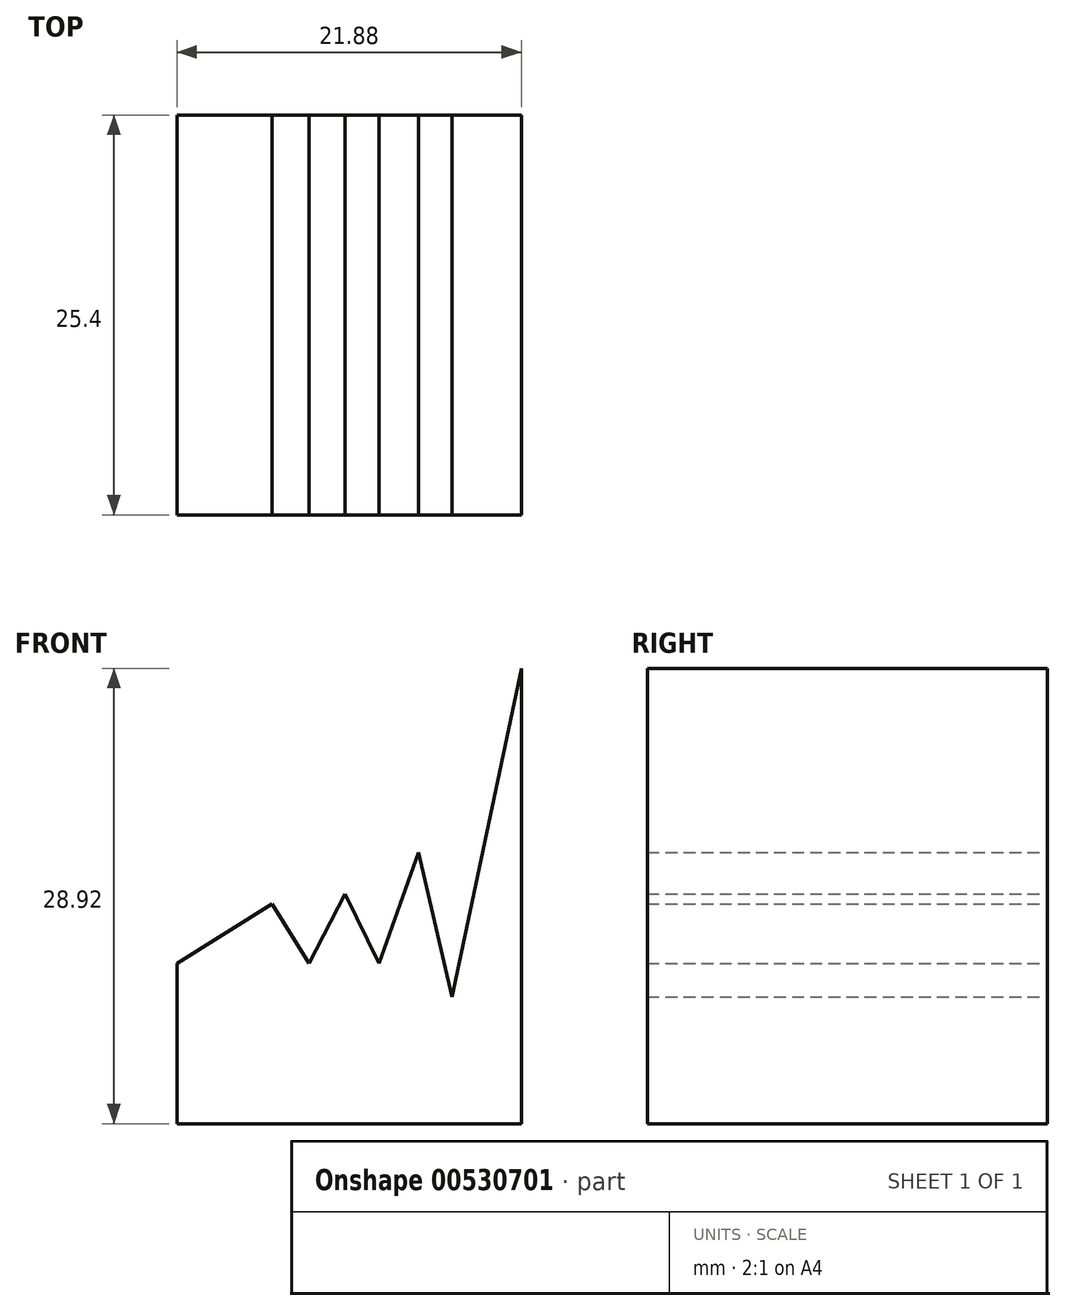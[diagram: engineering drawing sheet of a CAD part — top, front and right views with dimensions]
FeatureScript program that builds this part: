
annotation { "Feature Type Name" : "Feature", "Feature Type Description" : "" }
export const myFeature = defineFeature(function(context is Context, id is Id, definition is map)
    precondition{}
    {
        {
            var Q0;
            Q0=qCreatedBy(makeId("Front.planeOp"),FACE);
            var sketch = newSketch(context, id + "F0", { "sketchPlane" : qUnion([Q0])});
            skLineSegment(sketch, "E0", {"start": v(0, 0) * mm, "end": v(-57.46, 0) * mm});
            skLineSegment(sketch, "E1", {"start": v(0, 12.7) * mm, "end": v(-21.88, 12.7) * mm});
            skLineSegment(sketch, "E2", {"start": v(-21.88, 12.7) * mm, "end": v(-21.88, 22.89) * mm});
            skLineSegment(sketch, "E3", {"start": v(-21.88, 22.89) * mm, "end": v(-15.84, 26.66) * mm});
            skLineSegment(sketch, "E4", {"start": v(-15.84, 26.66) * mm, "end": v(-13.49, 22.89) * mm});
            skLineSegment(sketch, "E5", {"start": v(-13.49, 22.89) * mm, "end": v(-11.2, 27.29) * mm});
            skLineSegment(sketch, "E6", {"start": v(-11.2, 27.29) * mm, "end": v(-9.05, 22.89) * mm});
            skLineSegment(sketch, "E7", {"start": v(-9.05, 22.89) * mm, "end": v(-6.54, 29.93) * mm});
            skLineSegment(sketch, "E8", {"start": v(-6.54, 29.93) * mm, "end": v(-4.4, 20.75) * mm});
            skLineSegment(sketch, "E9", {"start": v(-4.4, 20.75) * mm, "end": v(0, 41.62) * mm});
            skLineSegment(sketch, "E10", {"start": v(0, 41.62) * mm, "end": v(0, 12.7) * mm});
            skSolve(sketch);
        }
        {
            var Q0;
            Q0=makeQuery(id+"F0.imprint","IMPRINT",FACE,{"disambiguationData":[TD([[makeQuery(id+"F0.imprint","IMPRINT",EDGE,{"derivedFrom":sQuery(id+"F0.wireOp",EDGE,"E1")}),-1.0]])]});
            extrude(context, id + "F1", {"entities" : qUnion([Q0]), "depth" : 25.4 * mm, "offsetDistance" : 25.4 * mm});
        }
    });
